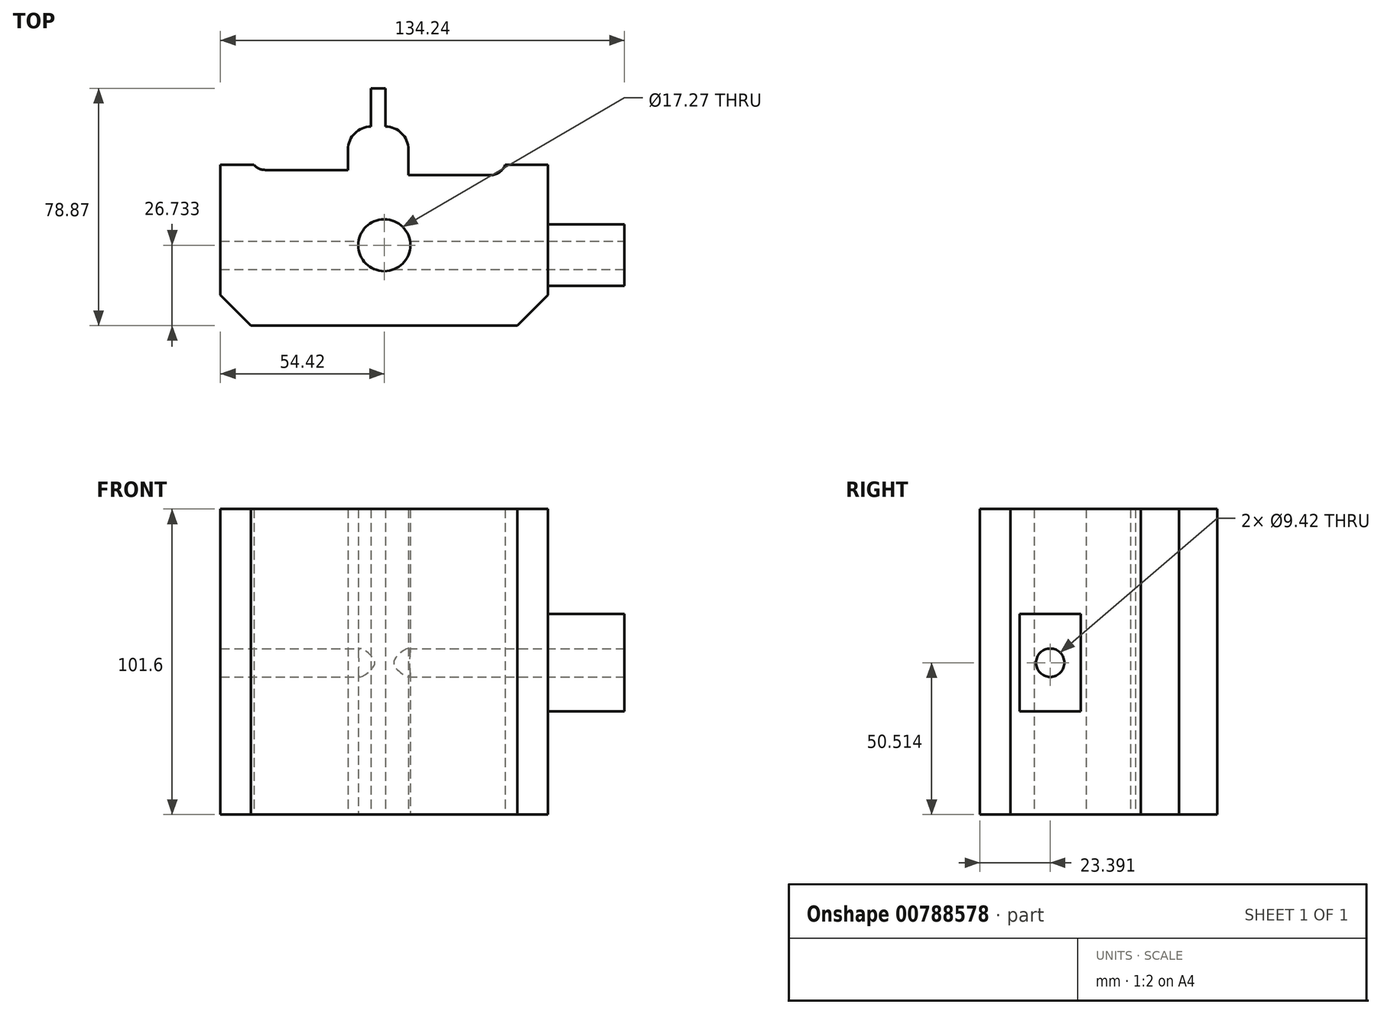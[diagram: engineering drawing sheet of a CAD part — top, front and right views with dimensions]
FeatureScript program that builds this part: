
annotation { "Feature Type Name" : "Feature", "Feature Type Description" : "" }
export const myFeature = defineFeature(function(context is Context, id is Id, definition is map)
    precondition{}
    {
        {
            var Q0;
            Q0=qCreatedBy(makeId("Top.planeOp"),FACE);
            var sketch = newSketch(context, id + "F0", { "sketchPlane" : qUnion([Q0])});
            skLineSegment(sketch, "E0.bottom", {"start": v(-44.4, 30.27) * mm, "end": v(-13.08, 30.27) * mm});
            skLineSegment(sketch, "E0.top", {"start": v(-44.4, 12.5) * mm, "end": v(-13.08, 12.5) * mm});
            skLineSegment(sketch, "E0.left", {"start": v(-44.4, 30.27) * mm, "end": v(-44.4, 12.5) * mm});
            skLineSegment(sketch, "E0.right", {"start": v(-13.08, 30.27) * mm, "end": v(-13.08, 12.5) * mm});
            skLineSegment(sketch, "E1.bottom", {"start": v(6.97, 30.65) * mm, "end": v(39.05, 30.65) * mm});
            skLineSegment(sketch, "E1.top", {"start": v(6.97, 10.79) * mm, "end": v(39.05, 10.79) * mm});
            skLineSegment(sketch, "E1.left", {"start": v(6.97, 30.65) * mm, "end": v(6.97, 10.79) * mm});
            skLineSegment(sketch, "E1.right", {"start": v(39.05, 30.65) * mm, "end": v(39.05, 10.79) * mm});
            skLineSegment(sketch, "E2.bottom", {"start": v(-55.47, 14.23) * mm, "end": v(53.37, 14.23) * mm});
            skLineSegment(sketch, "E2.top", {"start": v(-55.47, -39.24) * mm, "end": v(53.37, -39.24) * mm});
            skLineSegment(sketch, "E2.left", {"start": v(-55.47, 14.23) * mm, "end": v(-55.47, -39.24) * mm});
            skLineSegment(sketch, "E2.right", {"start": v(53.37, 14.23) * mm, "end": v(53.37, -39.24) * mm});
            skSolve(sketch);
        }
        {
            var Q0;
            {var subQ9=sQuery(id+"F0.wireOp",EDGE,"E0.top");Q0=makeQuery(id+"F0.imprint","IMPRINT",FACE,{"disambiguationData":[TD([[makeQuery(id+"F0.imprint","IMPRINT",EDGE,{"derivedFrom":subQ9}),-1.0]])]});}
            extrude(context, id + "F1", {"entities" : qUnion([Q0]), "endBound" : BoundingType.SYMMETRIC, "depth" : 101.6 * mm, "offsetDistance" : 25.4 * mm});
        }
        {
            var Q0;
            {var subQ0=sQuery(id+"F0.wireOp",EDGE,"E2.bottom");Q0=makeQuery(id+"F1.opExtrude","SWEPT_FACE",FACE,{"disambiguationData":[OSD([subQ0]),TDD([makeQuery(id+"F0.imprint","IMPRINT",EDGE,{"disambiguationData":[TD([[makeQuery(id+"F0.imprint","INTERSECT",VERTEX,{"derivedFrom":[sQuery(id+"F0.wireOp",EDGE,"E0.right"),subQ0]}),-1.0]])],"derivedFrom":subQ0})])]});}
            extrude(context, id + "F2", {"entities" : qUnion([Q0]), "operationType" : NewBodyOperationType.ADD, "depth" : 12.7 * mm, "offsetDistance" : 25.4 * mm});
        }
        {
            var Q0;
            {var subQ0=sQuery(id+"F0.wireOp",EDGE,"E2.bottom");var subQ1=sQuery(id+"F0.wireOp",EDGE,"E0.right");var subQ2=sQuery(id+"F0.wireOp",EDGE,"E1.left");Q0=makeQuery(id+"F2.boolean.opBoolean","MERGE",FACE,{"derivedFrom":[makeQuery(id+"F1.opExtrude","CAP_FACE",FACE,{"disambiguationData":[OSD([sQuery(id+"F0.wireOp",EDGE,"E0.top"),sQuery(id+"F0.wireOp",EDGE,"E0.left"),subQ1,sQuery(id+"F0.wireOp",EDGE,"E1.top"),subQ2,sQuery(id+"F0.wireOp",EDGE,"E1.right"),subQ0,sQuery(id+"F0.wireOp",EDGE,"E2.top"),sQuery(id+"F0.wireOp",EDGE,"E2.left"),sQuery(id+"F0.wireOp",EDGE,"E2.right")])],"isStart":true}),makeQuery(id+"F2.opExtrude","SWEPT_FACE",FACE,{"disambiguationData":[OSD([subQ0]),TDD([makeQuery(id+"F1.opExtrude","CAP_EDGE",EDGE,{"disambiguationData":[OSD([subQ0]),TDD([makeQuery(id+"F0.imprint","IMPRINT",EDGE,{"disambiguationData":[TD([[makeQuery(id+"F0.imprint","INTERSECT",VERTEX,{"derivedFrom":[subQ1,subQ0]}),-1.0]])],"derivedFrom":subQ0})])],"isStart":true})])]})]});}
            var sketch = newSketch(context, id + "F3", { "sketchPlane" : qUnion([Q0])});
            skLineSegment(sketch, "E3", {"start": v(53.37, -14.23) * mm, "end": v(-55.47, 39.24) * mm});
            skLineSegment(sketch, "E4", {"start": v(53.37, 39.24) * mm, "end": v(-55.47, -14.23) * mm});
            skCircle(sketch, "E5", {"center": v(-1.05, 12.5) * mm, "radius": 8.66 * mm});
            skSolve(sketch);
        }
        {
            var Q0;
            Q0=sQuery(id+"F3.wireOp",VERTEX,"E5.center");
            var Q1;
            Q1=makeQuery(id+"F1.opExtrude","SWEPT_BODY",BODY,{"disambiguationData":[OSD([sQuery(id+"F0.wireOp",EDGE,"E0.top"),sQuery(id+"F0.wireOp",EDGE,"E0.left"),sQuery(id+"F0.wireOp",EDGE,"E0.right"),sQuery(id+"F0.wireOp",EDGE,"E1.top"),sQuery(id+"F0.wireOp",EDGE,"E1.left"),sQuery(id+"F0.wireOp",EDGE,"E1.right"),sQuery(id+"F0.wireOp",EDGE,"E2.bottom"),sQuery(id+"F0.wireOp",EDGE,"E2.top"),sQuery(id+"F0.wireOp",EDGE,"E2.left"),sQuery(id+"F0.wireOp",EDGE,"E2.right")])]});
            hole(context, id + "F4", {"style" : HoleStyle.SIMPLE, "endStyle" : HoleEndStyle.THROUGH, "holeDiameter" : 17.27 * mm, "majorDiameter" : 6.35 * mm, "isTappedThrough" : true, "tappedDepth" : 12.7 * mm, "tapClearance" : 3, "locations" : qUnion([Q0]), "scope" : qUnion([Q1])});
        }
        {
            var Q0;
            {var subQ0=sQuery(id+"F0.wireOp",EDGE,"E2.bottom");var subQ1=sQuery(id+"F0.wireOp",EDGE,"E0.right");var subQ2=sQuery(id+"F0.wireOp",EDGE,"E1.left");Q0=makeQuery(id+"F2.boolean.opBoolean","MERGE",FACE,{"derivedFrom":[makeQuery(id+"F1.opExtrude","CAP_FACE",FACE,{"disambiguationData":[OSD([sQuery(id+"F0.wireOp",EDGE,"E0.top"),sQuery(id+"F0.wireOp",EDGE,"E0.left"),subQ1,sQuery(id+"F0.wireOp",EDGE,"E1.top"),subQ2,sQuery(id+"F0.wireOp",EDGE,"E1.right"),subQ0,sQuery(id+"F0.wireOp",EDGE,"E2.top"),sQuery(id+"F0.wireOp",EDGE,"E2.left"),sQuery(id+"F0.wireOp",EDGE,"E2.right")])],"isStart":false}),makeQuery(id+"F2.opExtrude","SWEPT_FACE",FACE,{"disambiguationData":[OSD([subQ0]),TDD([makeQuery(id+"F1.opExtrude","CAP_EDGE",EDGE,{"disambiguationData":[OSD([subQ0]),TDD([makeQuery(id+"F0.imprint","IMPRINT",EDGE,{"disambiguationData":[TD([[makeQuery(id+"F0.imprint","INTERSECT",VERTEX,{"derivedFrom":[subQ1,subQ0]}),-1.0]])],"derivedFrom":subQ0})])],"isStart":false})])]})]});}
            extrude(context, id + "F5", {"entities" : qUnion([Q0]), "operationType" : NewBodyOperationType.ADD, "depth" : -76.2 * mm, "offsetDistance" : 25.4 * mm});
        }
        {
            var Q0;
            {var subQ0=sQuery(id+"F0.wireOp",EDGE,"E2.bottom");var subQ1=sQuery(id+"F0.wireOp",EDGE,"E0.right");var subQ2=sQuery(id+"F0.wireOp",EDGE,"E1.left");Q0=makeQuery(id+"F2.boolean.opBoolean","MERGE",FACE,{"derivedFrom":[makeQuery(id+"F1.opExtrude","CAP_FACE",FACE,{"disambiguationData":[OSD([sQuery(id+"F0.wireOp",EDGE,"E0.top"),sQuery(id+"F0.wireOp",EDGE,"E0.left"),subQ1,sQuery(id+"F0.wireOp",EDGE,"E1.top"),subQ2,sQuery(id+"F0.wireOp",EDGE,"E1.right"),subQ0,sQuery(id+"F0.wireOp",EDGE,"E2.top"),sQuery(id+"F0.wireOp",EDGE,"E2.left"),sQuery(id+"F0.wireOp",EDGE,"E2.right")])],"isStart":false}),makeQuery(id+"F2.opExtrude","SWEPT_FACE",FACE,{"disambiguationData":[OSD([subQ0]),TDD([makeQuery(id+"F1.opExtrude","CAP_EDGE",EDGE,{"disambiguationData":[OSD([subQ0]),TDD([makeQuery(id+"F0.imprint","IMPRINT",EDGE,{"disambiguationData":[TD([[makeQuery(id+"F0.imprint","INTERSECT",VERTEX,{"derivedFrom":[subQ1,subQ0]}),-1.0]])],"derivedFrom":subQ0})])],"isStart":false})])]})]});}
            extrude(context, id + "F6", {"entities" : qUnion([Q0]), "operationType" : NewBodyOperationType.ADD, "depth" : -76.2 * mm, "offsetDistance" : 25.4 * mm});
        }
        {
            var Q0;
            Q0=makeQuery(id+"F1.opExtrude","SWEPT_FACE",FACE,{"disambiguationData":[OSD([sQuery(id+"F0.wireOp",EDGE,"E2.right")])]});
            var sketch = newSketch(context, id + "F7", { "sketchPlane" : qUnion([Q0])});
            skLineSegment(sketch, "E6.bottom", {"start": v(-26.07, 15.94) * mm, "end": v(-5.63, 15.94) * mm});
            skLineSegment(sketch, "E6.top", {"start": v(-26.07, -16.52) * mm, "end": v(-5.63, -16.52) * mm});
            skLineSegment(sketch, "E6.left", {"start": v(-26.07, 15.94) * mm, "end": v(-26.07, -16.52) * mm});
            skLineSegment(sketch, "E6.right", {"start": v(-5.63, 15.94) * mm, "end": v(-5.63, -16.52) * mm});
            skSolve(sketch);
        }
        {
            var Q0;
            Q0=makeQuery(id+"F7.imprint","IMPRINT",FACE,{"disambiguationData":[TD([[makeQuery(id+"F7.imprint","IMPRINT",EDGE,{"derivedFrom":sQuery(id+"F7.wireOp",EDGE,"E6.bottom")}),-1.0]])]});
            extrude(context, id + "F8", {"entities" : qUnion([Q0]), "operationType" : NewBodyOperationType.ADD, "depth" : 25.4 * mm, "offsetDistance" : 25.4 * mm});
        }
        {
            var Q0;
            Q0=makeQuery(id+"F2.opExtrude","CAP_EDGE",EDGE,{"disambiguationData":[OSD([sQuery(id+"F0.wireOp",EDGE,"E0.right"),sQuery(id+"F0.wireOp",EDGE,"E2.bottom")])],"isStart":false});
            var Q1;
            Q1=makeQuery(id+"F2.opExtrude","CAP_EDGE",EDGE,{"disambiguationData":[OSD([sQuery(id+"F0.wireOp",EDGE,"E1.left"),sQuery(id+"F0.wireOp",EDGE,"E2.bottom")])],"isStart":false});
            fillet(context, id + "F9", {"entities" : qUnion([Q0, Q1]), "radius" : 7.62 * mm, "tangentPropagation" : true, "allowEdgeOverflow" : false});
        }
        {
            var Q0;
            Q0=makeQuery(id+"F1.opExtrude","SWEPT_EDGE",EDGE,{"disambiguationData":[OSD([sQuery(id+"F0.wireOp",EDGE,"E2.top"),sQuery(id+"F0.wireOp",EDGE,"E2.right")])]});
            var Q1;
            Q1=makeQuery(id+"F1.opExtrude","SWEPT_EDGE",EDGE,{"disambiguationData":[OSD([sQuery(id+"F0.wireOp",EDGE,"E2.top"),sQuery(id+"F0.wireOp",EDGE,"E2.left")])]});
            chamfer(context, id + "F10", {"entities" : qUnion([Q0, Q1]), "width" : 10.16 * mm, "tangentPropagation" : true});
        }
        {
            var Q0;
            Q0=makeQuery(id+"F8.opExtrude","CAP_FACE",FACE,{"disambiguationData":[OSD([sQuery(id+"F7.wireOp",EDGE,"E6.bottom"),sQuery(id+"F7.wireOp",EDGE,"E6.top"),sQuery(id+"F7.wireOp",EDGE,"E6.left"),sQuery(id+"F7.wireOp",EDGE,"E6.right")])],"isStart":false});
            var sketch = newSketch(context, id + "F11", { "sketchPlane" : qUnion([Q0])});
            skLineSegment(sketch, "E7", {"start": v(-5.63, 15.94) * mm, "end": v(-26.07, -16.52) * mm});
            skLineSegment(sketch, "E8", {"start": v(-26.07, 15.94) * mm, "end": v(-5.63, -16.52) * mm});
            skCircle(sketch, "E9", {"center": v(-15.85, -0.29) * mm, "radius": 4.7 * mm});
            skSolve(sketch);
        }
        {
            var Q0;
            Q0=sQuery(id+"F11.wireOp",VERTEX,"E9.center");
            var Q1;
            Q1=makeQuery(id+"F1.opExtrude","SWEPT_BODY",BODY,{"disambiguationData":[OSD([sQuery(id+"F0.wireOp",EDGE,"E0.top"),sQuery(id+"F0.wireOp",EDGE,"E0.left"),sQuery(id+"F0.wireOp",EDGE,"E0.right"),sQuery(id+"F0.wireOp",EDGE,"E1.top"),sQuery(id+"F0.wireOp",EDGE,"E1.left"),sQuery(id+"F0.wireOp",EDGE,"E1.right"),sQuery(id+"F0.wireOp",EDGE,"E2.bottom"),sQuery(id+"F0.wireOp",EDGE,"E2.top"),sQuery(id+"F0.wireOp",EDGE,"E2.left"),sQuery(id+"F0.wireOp",EDGE,"E2.right")])]});
            hole(context, id + "F12", {"style" : HoleStyle.SIMPLE, "endStyle" : HoleEndStyle.THROUGH, "holeDiameter" : 9.42 * mm, "majorDiameter" : 6.35 * mm, "isTappedThrough" : true, "tappedDepth" : 12.7 * mm, "tapClearance" : 3, "locations" : qUnion([Q0]), "scope" : qUnion([Q1])});
        }
        {
            var Q0;
            Q0=makeQuery(id+"F2.opExtrude","CAP_FACE",FACE,{"disambiguationData":[OSD([sQuery(id+"F0.wireOp",EDGE,"E2.bottom")])],"isStart":false});
            extrude(context, id + "F13", {"entities" : qUnion([Q0]), "operationType" : NewBodyOperationType.ADD, "depth" : 12.7 * mm, "offsetDistance" : 25.4 * mm});
        }
        {
            var Q0;
            Q0=makeQuery(id+"F1.opExtrude","SWEPT_EDGE",EDGE,{"disambiguationData":[OSD([sQuery(id+"F0.wireOp",EDGE,"E0.top"),sQuery(id+"F0.wireOp",EDGE,"E0.left")])]});
            var Q1;
            Q1=makeQuery(id+"F1.opExtrude","SWEPT_EDGE",EDGE,{"disambiguationData":[OSD([sQuery(id+"F0.wireOp",EDGE,"E1.top"),sQuery(id+"F0.wireOp",EDGE,"E1.right")])]});
            fillet(context, id + "F14", {"entities" : qUnion([Q0, Q1]), "radius" : 5.08 * mm, "tangentPropagation" : true, "allowEdgeOverflow" : false});
        }
    });
